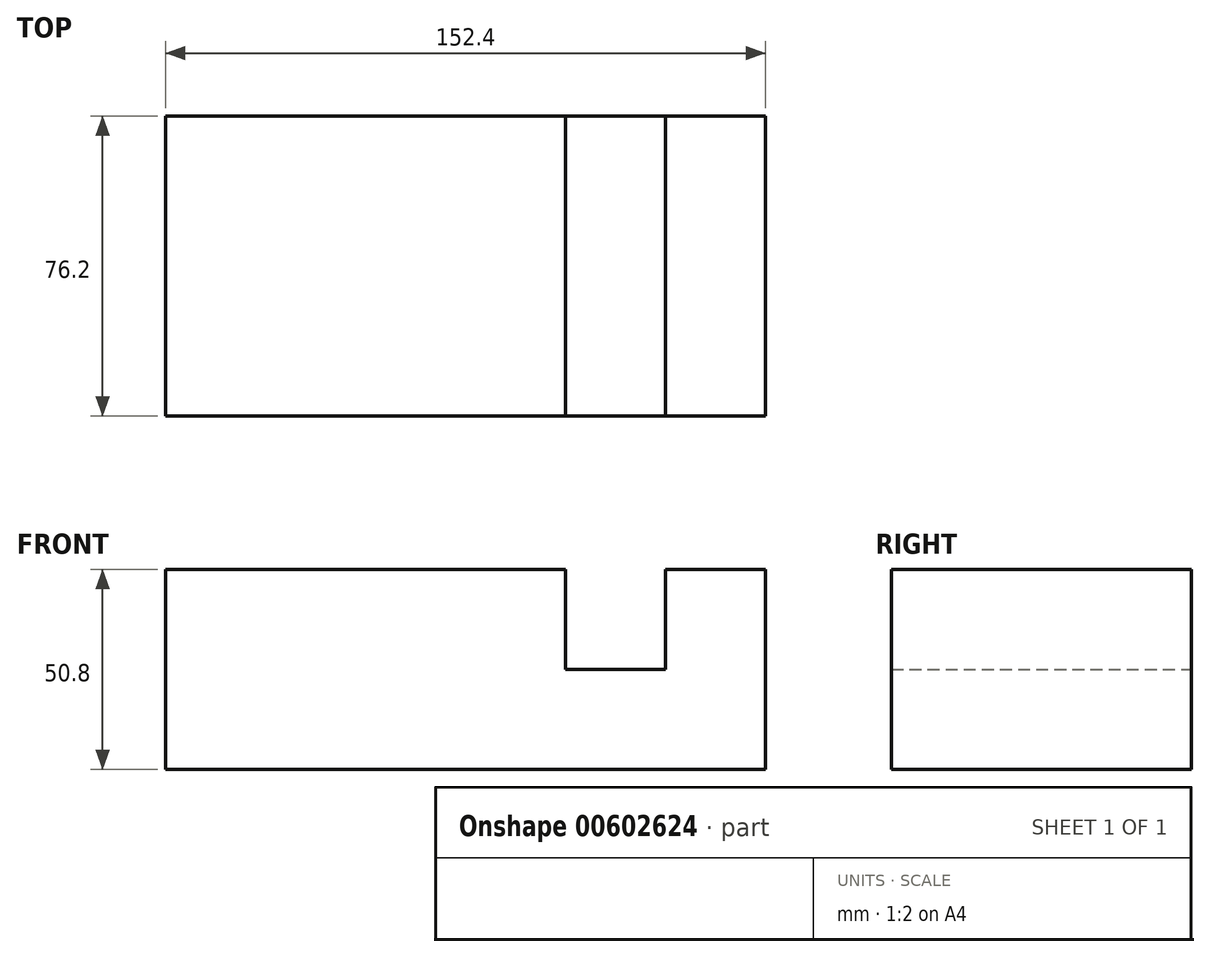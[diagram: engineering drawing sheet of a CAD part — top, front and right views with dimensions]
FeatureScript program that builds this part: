
annotation { "Feature Type Name" : "Feature", "Feature Type Description" : "" }
export const myFeature = defineFeature(function(context is Context, id is Id, definition is map)
    precondition{}
    {
        {
            var Q0;
            Q0=qCreatedBy(makeId("Front.planeOp"),FACE);
            var sketch = newSketch(context, id + "F0", { "sketchPlane" : qUnion([Q0])});
            skLineSegment(sketch, "E0", {"start": v(0, 0) * mm, "end": v(152.4, 0) * mm});
            skLineSegment(sketch, "E1", {"start": v(152.4, 0) * mm, "end": v(152.4, 50.8) * mm});
            skLineSegment(sketch, "E2", {"start": v(152.4, 50.8) * mm, "end": v(127, 50.8) * mm});
            skLineSegment(sketch, "E3", {"start": v(127, 50.8) * mm, "end": v(127, 25.4) * mm});
            skLineSegment(sketch, "E4", {"start": v(127, 25.4) * mm, "end": v(101.6, 25.4) * mm});
            skLineSegment(sketch, "E5", {"start": v(101.6, 25.4) * mm, "end": v(101.6, 50.8) * mm});
            skLineSegment(sketch, "E6", {"start": v(101.6, 50.8) * mm, "end": v(76.2, 50.8) * mm});
            skLineSegment(sketch, "E7", {"start": v(76.2, 50.8) * mm, "end": v(0, 50.8) * mm});
            skLineSegment(sketch, "E8", {"start": v(0, 50.8) * mm, "end": v(0, 0) * mm});
            skSolve(sketch);
        }
        {
            var Q0;
            Q0 = qSketchRegion(id + "F0", true);
            extrude(context, id + "F1", {"entities" : qUnion([Q0]), "depth" : 76.2 * mm, "offsetDistance" : 25.4 * mm});
        }
    });
